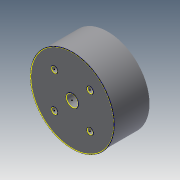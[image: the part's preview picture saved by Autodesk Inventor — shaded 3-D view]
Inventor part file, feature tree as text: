
AUTODESK INVENTOR PART (.ipt)
format: ipt  version: 2015 (Build 190159000, 159)  size: 110,080 bytes
history: native  units: mm
features: other x8, extrude x1, sketch x1, projected_geometry x1
ambient origin geometry x8: Origin, YZ Plane, XZ Plane, XY Plane, X Axis, Y Axis, Z Axis, Center Point
bodies: Body1 (feature_tree)
feature tree (11):
  other  "Blocks"
  extrude  "Extrusion5"  Depth=5.0mm
  sketch  "Sketch9"  dims[d0=70.0mm d29=5.0mm d30=15.0mm d31=15.0mm d34=10.0mm d35=30.0mm d36=0.0mm]
  other  "DXF"
  other  "Block1"
  other  "Block2"
  other  "Block3"
  projected_geometry  "Projected Loop3"
  other  "Block4"
  other  "Block4:1"
  other  "Block4:2"
